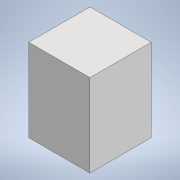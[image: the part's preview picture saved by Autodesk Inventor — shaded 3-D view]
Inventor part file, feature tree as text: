
AUTODESK INVENTOR PART (.ipt)
format: ipt  version: 2022.3 (Build 263350000, 350)  size: 189,952 bytes
history: native  units: mm
features: extrude x5, sketch x5, fillet x1, hole x1
ambient origin geometry x8: Origin, YZ Plane, XZ Plane, XY Plane, X Axis, Y Axis, Z Axis, Center Point
bodies: Solid1 (feature_tree)
feature tree (12):
  extrude  "Extrusion1"  Depth=60.0mm
  extrude  "Extrusion2"  Depth=4.0mm
  sketch  "Sketch3"  dims[d5=25.0mm d6=8.0mm]
  extrude  "Extrusion3"  Depth=25.0mm
  extrude  "Extrusion4"  Depth=42.0mm
  fillet  "Fillet1"  Radius=51.0mm
  extrude  "Extrusion5"  Depth=4.0mm
  hole  "Hole1"  [1 undecoded]
  sketch  "Sketch1"  dims[d0=50.0mm d1=60.0mm]
  sketch  "Sketch2"  dims[d2=53.0mm d3=0.0mm d4=4.0mm]
  sketch  "Sketch4"  dims[d7=37.5mm d8=42.0mm d9=51.0mm d10=0.0mm]
  sketch  "Sketch5"  dims[d11=17.5mm d12=35.0mm d13=15.0mm d14=15.0mm d15=37.0mm d16=0.0mm d17=13.0mm d18=0.0mm d19=4.0mm d20=18.0mm d21=22.0mm d22=0.0mm d23=0.0mm d24=42.0mm d25=90.0deg d26=31.0mm d27=31.0mm d28=2.4mm d29=6.0mm d30=4.0mm d31=2.0mm d32=90.0deg d33=4.0mm d34=0.0mm]
note: 1 required parameter value undecoded (feature->parameter linkage not recoverable at this tier; creation-order binding heuristic only, values carry confidence <= 0.55)
